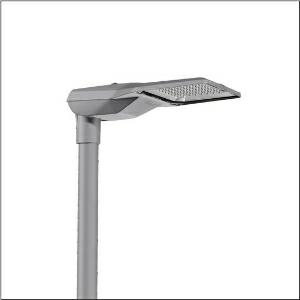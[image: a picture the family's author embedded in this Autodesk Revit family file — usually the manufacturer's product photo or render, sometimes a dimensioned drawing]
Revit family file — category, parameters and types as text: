
# Revit family: streetlight_sl_21_midi___pl52_5xe3h43s08mb_aca6
name_source: partatom
category: Lighting Fixtures
units: mm (PartAtom-declared; Revit-internal decimal feet)

## family parameters
Cut with Voids When Loaded = No
Host = Face
Light Source = No
Part Type = Normal
Room Calculation Point = No
Round Connector Dimension = Use Diameter
Shared = No

## types (1)
- --- (1 x LED, 19830 lm, 147 W, 4000K)
    Apparent Load = 147 VA
    CIE Flux Codes = 27 59 98 100 100
    Color Rendering = 70
    Color Temperature = 4000K
    Default Elevation = 1800 mm
    Description = Streetlight SL 21 midi, mast luminaire, primary light control with lens, of PMMA, primary optical cover: cover, of toughened safety glass, transparent, light distribution: PL52, light emission: direct distribution, primary light characteristic: asymmetric, installation type: side-entry, post-top, LED, High Power LED, rated luminous flux: 19.830lm, luminous efficacy: 135lm/W, light colour: 740, colour temperature: 4000K, control gear: D4i, control: overheat protection, constant luminous flux control, time-dependent luminous flux control, flexible luminous flux parameterisation, pre-setting: logarithmic dimming characteristic, mains connection: 230..240V, AC, 50/60Hz, start of lifetime: 147W, end of service life: 155W, reduction: 65W, luminaire housing, of diecast aluminium, powder-coated, Siteco® metallic grey (DB 702S), corrosivity category C5 mid according to DIN EN ISO 12944, please order mast flange separately, inclination adjustable: 0°, 5°, 10°, 15°, sealing non-destructively replaceable, multi-level sealing system, length: 644mm, width: 335mm, height: 110mm, mast flange for spigot size: 42mm (side-entry): 5XC10008XM4, 60/48mm (side-entry/post-top): 5XC10108XM2, 76/60mm (side-entry/post-top): 5XC10108XM1, mounting height: 4..8m, Smart Interface above, protection rating (complete): IP66, insulation class (complete): insulation class II (safety insulation), certification: CE, ENEC, ENEC+, VDE, impact resistance: IK10, permissible operating ambient temperature for outdoor applications: -40..+50°C, standard-compliant lighting for roads and squares, packaging unit: 1 piece

Light Distribution: PL52
    Height = 111 mm
    Lamp = 1 x LED
    Lamp Light Flux = 19830 lm
    Lamp Power = 147 W
    Lamp count = 1
    Length = 644 mm
    Luminous efficacy = 135 lm/W
    Manufacturer = Siteco
    ModVariant = No
    Model = 5XE3H43S08MB
    Number of Poles = 1
    OnlyDefault = Yes
    Power Factor = 1
    Product Name = Streetlight SL 21 midi | PL52
    Product group = mast luminaire | pylon top
    ProductGroupID = 6100
    Protection Class = Protection class II
    Protection Degree = IP 66
    RLX_Detail_Level = 1
    RLX_Emergency_Light_Flux = 0 lm
    RLX_Emergency_Type = 0
    RLX_Emergency_Type_DB = No
    RlxData = <blob elided: 36385 chars, md5=202f1b2b>
    Socket = socket
    Standby Power = 0 W
    System Light Flux = 19830 lm
    System Power = 147 W
    Type Comments = factory setting: luminous flux: 100 % | dim-lin: 254 | 750 mA
    Type Image = l_1004302.jpg
    URL = http://relux.com
    VarID = @adj_211927
    Voltage = 0 V
    Weight = 0.00 kg
    Width = 336 mm

## geometry (parser evidence)
native form markers: Blend x4, Sweep x8
no freeform markers — native parametric forms only
